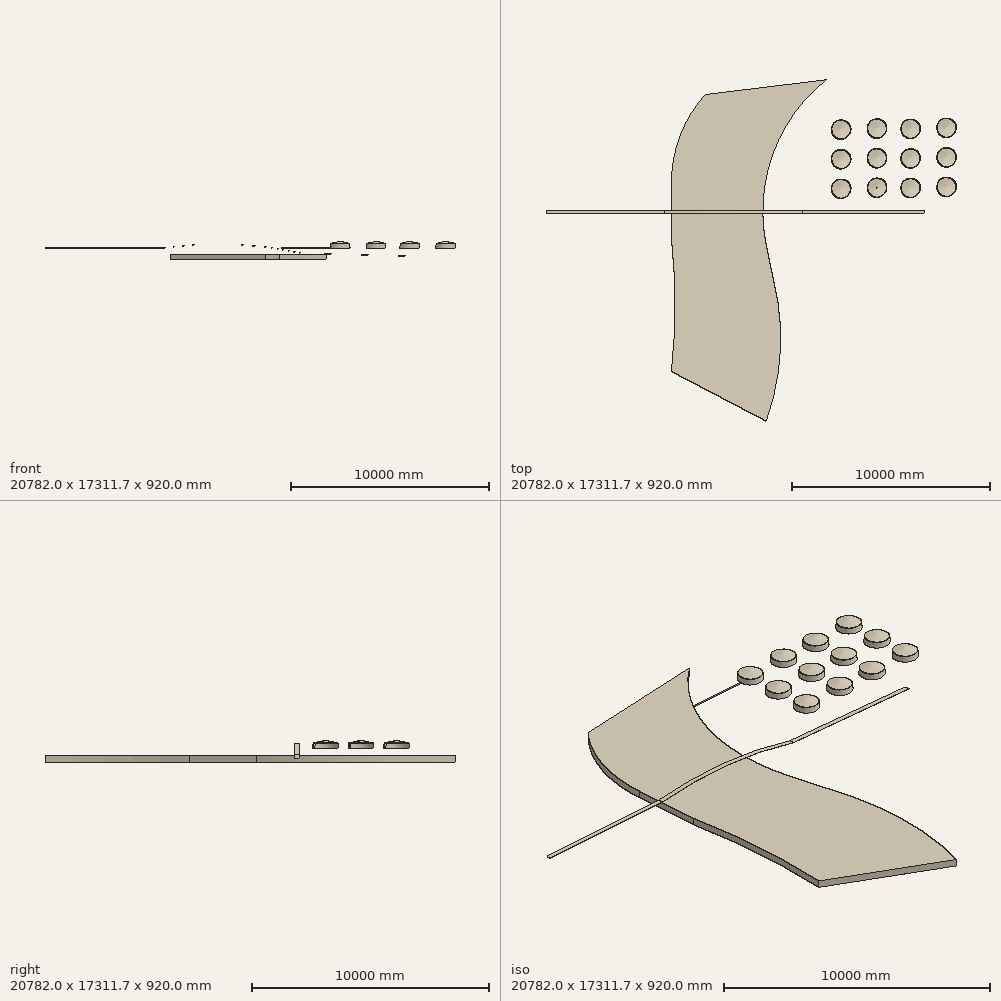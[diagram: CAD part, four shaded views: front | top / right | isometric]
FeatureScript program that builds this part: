
annotation { "Feature Type Name" : "Feature", "Feature Type Description" : "" }
export const myFeature = defineFeature(function(context is Context, id is Id, definition is map)
    precondition{}
    {
        {
            var Q0;
            Q0=qCreatedBy(makeId("Front.planeOp"),FACE);
            var sketch = newSketch(context, id + "F0", { "sketchPlane" : qUnion([Q0])});
            skLineSegment(sketch, "E0", {"start": v(-512.59, 0) * mm, "end": v(5487.41, 0) * mm});
            skLineSegment(sketch, "E1", {"start": v(5487.41, 10) * mm, "end": v(-512.59, 10) * mm});
            skLineSegment(sketch, "E2", {"start": v(-512.59, 10) * mm, "end": v(-512.59, 0) * mm});
            skArc(sketch, "E3", {"start": v(12473.91, -256.36) * mm, "mid": v(8993.12, 203.5) * mm, "end": v(5487.41, 10) * mm});
            skLineSegment(sketch, "E4", {"start": v(12473.91, -256.36) * mm, "end": v(18626.62, -422.67) * mm});
            skArc(sketch, "E5.0", {"start": v(12471.69, -266.1) * mm, "mid": v(8992.74, 193.5) * mm, "end": v(5488.9, 0.1) * mm});
            skLineSegment(sketch, "E6.0", {"start": v(12473.64, -266.36) * mm, "end": v(18626.62, -432.67) * mm});
            skLineSegment(sketch, "E7", {"start": v(18626.62, -422.67) * mm, "end": v(18626.62, -432.67) * mm});
            skLineSegment(sketch, "E8", {"start": v(12471.69, -266.1) * mm, "end": v(12473.64, -266.36) * mm});
            skLineSegment(sketch, "E9", {"start": v(5488.9, 0.1) * mm, "end": v(5487.41, 0) * mm});
            skSolve(sketch);
        }
        {
            var Q0;
            Q0 = qSketchRegion(id + "F0", true);
            extrude(context, id + "F1", {"entities" : qUnion([Q0]), "endBound" : BoundingType.SYMMETRIC, "depth" : 200 * mm});
        }
        {
            var Q0;
            Q0=qCreatedBy(makeId("Top.planeOp"),FACE);
            cPlane(context, id + "F2", {"entities" : qUnion([Q0]), "cplaneType" : CPlaneType.OFFSET, "offset" : 300 * mm, "oppositeDirection" : true, "width" : 150 * mm, "height" : 150 * mm});
        }
        {
            var Q0;
            Q0=qCreatedBy(id+"F2.planeOp",FACE);
            var sketch = newSketch(context, id + "F3", { "sketchPlane" : qUnion([Q0])});
            skLineSegment(sketch, "E10", {"start": v(5821.9, 1476.15) * mm, "end": v(5821.9, -1373.83) * mm});
            skLineSegment(sketch, "E11", {"start": v(10631.17, -1712.24) * mm, "end": v(11212.04, -4514.35) * mm});
            skArc(sketch, "E12", {"start": v(7552.86, 5952.19) * mm, "mid": v(6269.7, 3875.69) * mm, "end": v(5821.9, 1476.15) * mm});
            skArc(sketch, "E13", {"start": v(13707.41, 6704.02) * mm, "mid": v(10971, 2933.88) * mm, "end": v(10631.17, -1712.24) * mm});
            skArc(sketch, "E14", {"start": v(5821.9, -8087.9) * mm, "mid": v(6018.32, -4730.86) * mm, "end": v(5821.9, -1373.83) * mm});
            skArc(sketch, "E15", {"start": v(10631.17, -10607.69) * mm, "mid": v(11302.3, -7597.31) * mm, "end": v(11212.04, -4514.35) * mm});
            skLineSegment(sketch, "E16", {"start": v(7552.86, 5952.19) * mm, "end": v(13707.41, 6704.02) * mm});
            skLineSegment(sketch, "E17", {"start": v(10631.17, -10607.69) * mm, "end": v(5821.9, -8087.9) * mm});
            skSolve(sketch);
        }
        {
            var Q0;
            Q0 = qSketchRegion(id + "F3", true);
            extrude(context, id + "F4", {"entities" : qUnion([Q0]), "operationType" : NewBodyOperationType.ADD, "oppositeDirection" : true, "depth" : 280 * mm});
        }
        {
            var Q0;
            Q0=qCreatedBy(makeId("Top.planeOp"),FACE);
            var sketch = newSketch(context, id + "F5", { "sketchPlane" : qUnion([Q0])});
            skCircle(sketch, "E18", {"center": v(14424.1, 1171.28) * mm, "radius": 500 * mm});
            skCircle(sketch, "E19", {"center": v(14424.1, 2671.28) * mm, "radius": 500 * mm});
            skCircle(sketch, "E20", {"center": v(14424.1, 4171.28) * mm, "radius": 500 * mm});
            skCircle(sketch, "E21", {"center": v(16244.98, 1224.2) * mm, "radius": 500 * mm});
            skCircle(sketch, "E22", {"center": v(16244.98, 2724.2) * mm, "radius": 500 * mm});
            skCircle(sketch, "E23", {"center": v(16244.98, 4224.2) * mm, "radius": 500 * mm});
            skCircle(sketch, "E24", {"center": v(17948.48, 1210) * mm, "radius": 500 * mm});
            skCircle(sketch, "E25", {"center": v(17948.48, 2710) * mm, "radius": 500 * mm});
            skCircle(sketch, "E26", {"center": v(17948.48, 4210) * mm, "radius": 500 * mm});
            skCircle(sketch, "E27", {"center": v(19769.36, 1262.93) * mm, "radius": 500 * mm});
            skCircle(sketch, "E28", {"center": v(19769.36, 2762.93) * mm, "radius": 500 * mm});
            skCircle(sketch, "E29", {"center": v(19769.36, 4262.93) * mm, "radius": 500 * mm});
            skSolve(sketch);
        }
        {
            var Q0;
            Q0 = qSketchRegion(id + "F5", true);
            extrude(context, id + "F6", {"entities" : qUnion([Q0]), "depth" : 340 * mm, "hasDraft" : true, "draftAngle" : 5 * degree, "draftPullDirection" : true});
        }
        {
            var Q0;
            Q0=makeQuery(id+"F6.opExtrude","CAP_FACE",FACE,{"disambiguationData":[OSD([sQuery(id+"F5.wireOp",EDGE,"E20")])],"isStart":false});
            var Q1;
            Q1=makeQuery(id+"F6.opExtrude","CAP_FACE",FACE,{"disambiguationData":[OSD([sQuery(id+"F5.wireOp",EDGE,"E19")])],"isStart":false});
            var Q2;
            Q2=makeQuery(id+"F6.opExtrude","CAP_FACE",FACE,{"disambiguationData":[OSD([sQuery(id+"F5.wireOp",EDGE,"E18")])],"isStart":false});
            var Q3;
            Q3=makeQuery(id+"F6.opExtrude","CAP_FACE",FACE,{"disambiguationData":[OSD([sQuery(id+"F5.wireOp",EDGE,"E23")])],"isStart":false});
            var Q4;
            Q4=makeQuery(id+"F6.opExtrude","CAP_FACE",FACE,{"disambiguationData":[OSD([sQuery(id+"F5.wireOp",EDGE,"E22")])],"isStart":false});
            var Q5;
            Q5=makeQuery(id+"F6.opExtrude","CAP_FACE",FACE,{"disambiguationData":[OSD([sQuery(id+"F5.wireOp",EDGE,"E21")])],"isStart":false});
            var Q6;
            Q6=makeQuery(id+"F6.opExtrude","CAP_FACE",FACE,{"disambiguationData":[OSD([sQuery(id+"F5.wireOp",EDGE,"E26")])],"isStart":false});
            var Q7;
            Q7=makeQuery(id+"F6.opExtrude","CAP_FACE",FACE,{"disambiguationData":[OSD([sQuery(id+"F5.wireOp",EDGE,"E25")])],"isStart":false});
            var Q8;
            Q8=makeQuery(id+"F6.opExtrude","CAP_FACE",FACE,{"disambiguationData":[OSD([sQuery(id+"F5.wireOp",EDGE,"E24")])],"isStart":false});
            var Q9;
            Q9=makeQuery(id+"F6.opExtrude","CAP_FACE",FACE,{"disambiguationData":[OSD([sQuery(id+"F5.wireOp",EDGE,"E29")])],"isStart":false});
            var Q10;
            Q10=makeQuery(id+"F6.opExtrude","CAP_FACE",FACE,{"disambiguationData":[OSD([sQuery(id+"F5.wireOp",EDGE,"E28")])],"isStart":false});
            var Q11;
            Q11=makeQuery(id+"F6.opExtrude","CAP_FACE",FACE,{"disambiguationData":[OSD([sQuery(id+"F5.wireOp",EDGE,"E27")])],"isStart":false});
            chamfer(context, id + "F7", {"entities" : qUnion([Q0, Q1, Q2, Q3, Q4, Q5, Q6, Q7, Q8, Q9, Q10, Q11]), "chamferType" : ChamferType.OFFSET_ANGLE, "width" : 100 * mm, "oppositeDirection" : true, "angle" : 73 * degree, "tangentPropagation" : true});
        }
        {
            var Q0;
            {var subQ0=sQuery(id+"F5.wireOp",EDGE,"E20");Q0=makeQuery(id+"F7.opChamfer","BLEND_EDGE",EDGE,{"blendedFrom":[makeQuery(id+"F6.opExtrude","CAP_EDGE",EDGE,{"disambiguationData":[OSD([subQ0])],"isStart":false}),makeQuery(id+"F6.opExtrude","SWEPT_FACE",FACE,{"disambiguationData":[OSD([subQ0])]})],"blendedInto":[makeQuery(id+"F6.opExtrude","SWEPT_FACE",FACE,{"disambiguationData":[OSD([subQ0])]})]});}
            var Q1;
            Q1=makeQuery(id+"F7.opChamfer","BLEND_FACE",FACE,{"disambiguationData":[OSD([sQuery(id+"F5.wireOp",EDGE,"E19")])]});
            var Q2;
            Q2=makeQuery(id+"F7.opChamfer","BLEND_FACE",FACE,{"disambiguationData":[OSD([sQuery(id+"F5.wireOp",EDGE,"E18")])]});
            var Q3;
            Q3=makeQuery(id+"F7.opChamfer","BLEND_FACE",FACE,{"disambiguationData":[OSD([sQuery(id+"F5.wireOp",EDGE,"E21")])]});
            var Q4;
            Q4=makeQuery(id+"F7.opChamfer","BLEND_FACE",FACE,{"disambiguationData":[OSD([sQuery(id+"F5.wireOp",EDGE,"E22")])]});
            var Q5;
            Q5=makeQuery(id+"F7.opChamfer","BLEND_FACE",FACE,{"disambiguationData":[OSD([sQuery(id+"F5.wireOp",EDGE,"E23")])]});
            var Q6;
            Q6=makeQuery(id+"F7.opChamfer","BLEND_FACE",FACE,{"disambiguationData":[OSD([sQuery(id+"F5.wireOp",EDGE,"E26")])]});
            var Q7;
            Q7=makeQuery(id+"F7.opChamfer","BLEND_FACE",FACE,{"disambiguationData":[OSD([sQuery(id+"F5.wireOp",EDGE,"E25")])]});
            var Q8;
            Q8=makeQuery(id+"F7.opChamfer","BLEND_FACE",FACE,{"disambiguationData":[OSD([sQuery(id+"F5.wireOp",EDGE,"E24")])]});
            var Q9;
            Q9=makeQuery(id+"F7.opChamfer","BLEND_FACE",FACE,{"disambiguationData":[OSD([sQuery(id+"F5.wireOp",EDGE,"E29")])]});
            var Q10;
            Q10=makeQuery(id+"F7.opChamfer","BLEND_FACE",FACE,{"disambiguationData":[OSD([sQuery(id+"F5.wireOp",EDGE,"E28")])]});
            var Q11;
            Q11=makeQuery(id+"F7.opChamfer","BLEND_FACE",FACE,{"disambiguationData":[OSD([sQuery(id+"F5.wireOp",EDGE,"E27")])]});
            fillet(context, id + "F8", {"entities" : qUnion([Q0, Q1, Q2, Q3, Q4, Q5, Q6, Q7, Q8, Q9, Q10, Q11]), "radius" : 12.3 * mm, "tangentPropagation" : true, "rho" : 0.5, "crossSection" : FilletCrossSection.CONIC, "allowEdgeOverflow" : false});
        }
        {
            var Q0;
            Q0=qCreatedBy(makeId("Top.planeOp"),FACE);
            var sketch = newSketch(context, id + "F9", { "sketchPlane" : qUnion([Q0])});
            skLineSegment(sketch, "E30", {"start": v(11463.72, 4174.99) * mm, "end": v(13941.54, 4174.99) * mm});
            skSolve(sketch);
        }
        {
            var Q0;
            Q0=sQuery(id+"F9.wireOp",VERTEX,"E30.end");
            var Q1;
            Q1=sQuery(id+"F9.wireOp",EDGE,"E30");
            cPlane(context, id + "F10", {"entities" : qUnion([Q0, Q1]), "cplaneType" : CPlaneType.CURVE_POINT, "offset" : 25 * mm, "width" : 150 * mm, "height" : 150 * mm});
        }
        {
            var Q0;
            Q0=qCreatedBy(id+"F10.planeOp",FACE);
            var sketch = newSketch(context, id + "F11", { "sketchPlane" : qUnion([Q0])});
            skPoint(sketch, "E31.0", {"position": v(4174.99, 0) * mm});
            skCircle(sketch, "E32", {"center": v(4174.99, 0) * mm, "radius": 17.5 * mm});
            skSolve(sketch);
        }
        {
            var Q0;
            Q0=makeQuery(id+"F11.imprint","IMPRINT",FACE,{"disambiguationData":[TD([[makeQuery(id+"F11.imprint","IMPRINT",EDGE,{"derivedFrom":sQuery(id+"F11.wireOp",EDGE,"E32")}),1.0]])]});
            var Q1;
            Q1=sQuery(id+"F9.wireOp",EDGE,"E30");
            sweep(context, id + "F12", {"profiles" : qUnion([Q0]), "path" : qUnion([Q1])});
        }
    });
